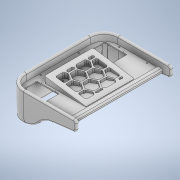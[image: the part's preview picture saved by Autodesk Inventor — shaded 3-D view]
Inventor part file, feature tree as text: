
AUTODESK INVENTOR PART (.ipt)
format: ipt  version: 2021 (Build 250183000, 183)  size: 1,799,168 bytes
history: native  units: mm
features: sketch x20, projected_geometry x14, extrude x12, fillet x7, other x6, plane x5, hole x4, mirror x3, loft x1, chamfer x1
ambient origin geometry x8: Origin, YZ Plane, XZ Plane, XY Plane, X Axis, Y Axis, Z Axis, Center Point
bodies: Body1 (feature_tree), Body2 (feature_tree), Body3 (feature_tree), Body4 (feature_tree)
feature tree (73):
  sketch  "草圖1"
  plane  "工作平面1"
  sketch  "草圖2"
  plane  "工作平面2"
  sketch  "草圖3"
  sketch  "草圖5"
  plane  "工作平面4"
  loft  "斷面混成3"
  plane  "工作平面3"
  extrude  "擠出2"  Depth=700.0mm
  fillet  "圓角8"  Radius=500.0mm
  fillet  "圓角9"  Radius=20.0mm
  fillet  "圓角10"  Radius=20.0mm
  plane  "工作平面5"
  chamfer  "倒角2"  Distance=100.0mm
  hole  "孔1"  [1 undecoded]
  extrude  "擠出3"  [1 undecoded]
  hole  "孔2"  [1 undecoded]
  extrude  "擠出4"  [1 undecoded]
  fillet  "圓角12"  [1 undecoded]
  extrude  "擠出6"  [1 undecoded]
  mirror  "鏡射1"
  hole  "孔3"  [1 undecoded]
  extrude  "擠出7"  TaperAngle=0.0deg  [1 undecoded]
  hole  "孔4"  [1 undecoded]
  fillet  "圓角13"  Radius=75.0mm
  mirror  "鏡射2"
  extrude  "擠出8"  Depth=10.0mm
  mirror  "鏡射3"
  extrude  "擠出9"  Depth=325.0mm
  extrude  "擠出10"  TaperAngle=0.0deg  [1 undecoded]
  extrude  "擠出11"  Depth=150.0mm
  sketch  "草圖23"
  extrude  "擠出12"  Depth=20.0mm
  extrude  "擠出13"  [1 undecoded]
  extrude  "擠出14"  Depth=20.0mm
  fillet  "圓角14"  Radius=85.451367mm
  fillet  "圓角15"  Radius=12.0mm
  sketch  "草圖6"
  other  "實體3"
  sketch  "草圖7"
  sketch  "草圖8"
  sketch  "草圖9"
  projected_geometry  "投影迴路1"
  sketch  "草圖10"
  projected_geometry  "投影迴路2"
  other  "實體4"
  sketch  "草圖11"
  projected_geometry  "投影迴路3"
  projected_geometry  "投影迴路4"
  projected_geometry  "投影迴路5"
  projected_geometry  "投影迴路6"
  projected_geometry  "投影迴路7"
  projected_geometry  "投影迴路8"
  sketch  "草圖12"
  other  "實體5"
  projected_geometry  "投影迴路10"
  sketch  "草圖15"
  sketch  "草圖16"
  sketch  "草圖17"
  sketch  "草圖18"
  projected_geometry  "投影迴路11"
  sketch  "草圖19"
  sketch  "草圖20"
  other  "實體6"
  sketch  "草圖21"
  projected_geometry  "投影迴路12"
  sketch  "草圖22"
  projected_geometry  "投影迴路13"
  projected_geometry  "投影迴路14"
  projected_geometry  "投影迴路15"
  other  "投影切割邊1"
  other  "投影切割邊2"
note: 11 required parameter values undecoded (feature->parameter linkage not recoverable at this tier; creation-order binding heuristic only, values carry confidence <= 0.55)
